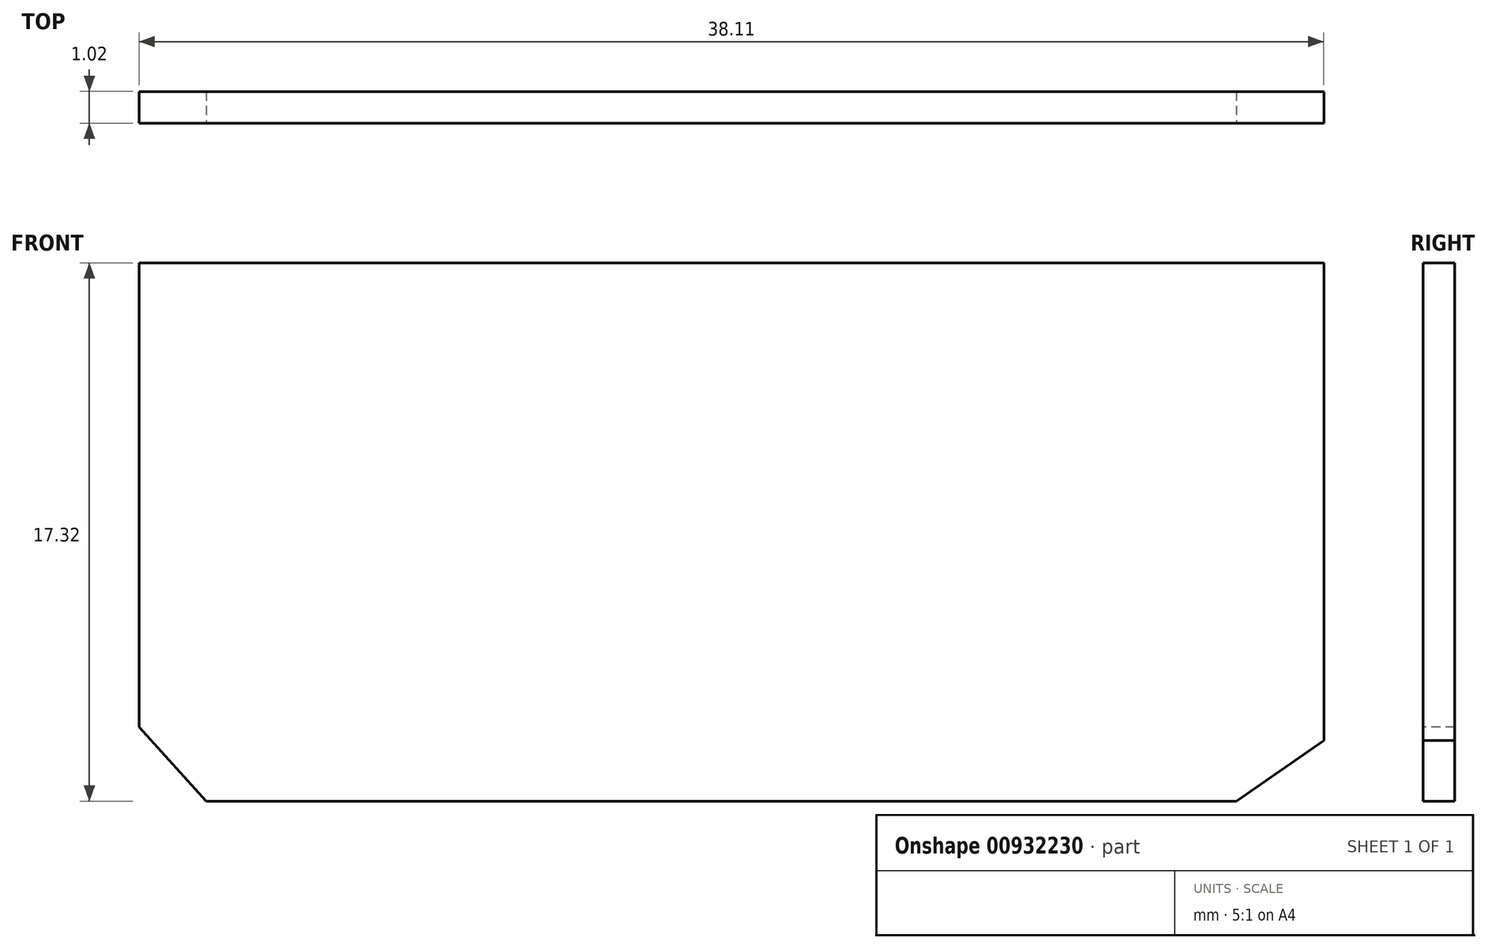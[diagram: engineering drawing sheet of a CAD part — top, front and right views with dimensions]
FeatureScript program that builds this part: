
annotation { "Feature Type Name" : "Feature", "Feature Type Description" : "" }
export const myFeature = defineFeature(function(context is Context, id is Id, definition is map)
    precondition{}
    {
        {
            var Q0;
            Q0=qCreatedBy(makeId("Front.planeOp"),FACE);
            var sketch = newSketch(context, id + "F0", { "sketchPlane" : qUnion([Q0])});
            skLineSegment(sketch, "E0", {"start": v(-50.13, 17.32) * mm, "end": v(-12.02, 17.32) * mm});
            skLineSegment(sketch, "E1", {"start": v(-50.13, 17.32) * mm, "end": v(-50.13, 2.38) * mm});
            skLineSegment(sketch, "E2", {"start": v(-50.13, 2.38) * mm, "end": v(-47.96, 0) * mm});
            skLineSegment(sketch, "E3", {"start": v(-47.96, 0) * mm, "end": v(-14.83, 0) * mm});
            skLineSegment(sketch, "E4", {"start": v(-12.02, 1.95) * mm, "end": v(-12.02, 17.32) * mm});
            skLineSegment(sketch, "E5", {"start": v(-14.83, 0) * mm, "end": v(-12.02, 1.95) * mm});
            skSolve(sketch);
        }
        {
            var Q0;
            Q0=makeQuery(id+"F0.imprint","IMPRINT",FACE,{"disambiguationData":[TD([[makeQuery(id+"F0.imprint","IMPRINT",EDGE,{"derivedFrom":sQuery(id+"F0.wireOp",EDGE,"E0")}),-1.0]])]});
            extrude(context, id + "F1", {"entities" : qUnion([Q0]), "oppositeDirection" : true, "depth" : 1.02 * mm, "offsetDistance" : 25.4 * mm});
        }
    });
